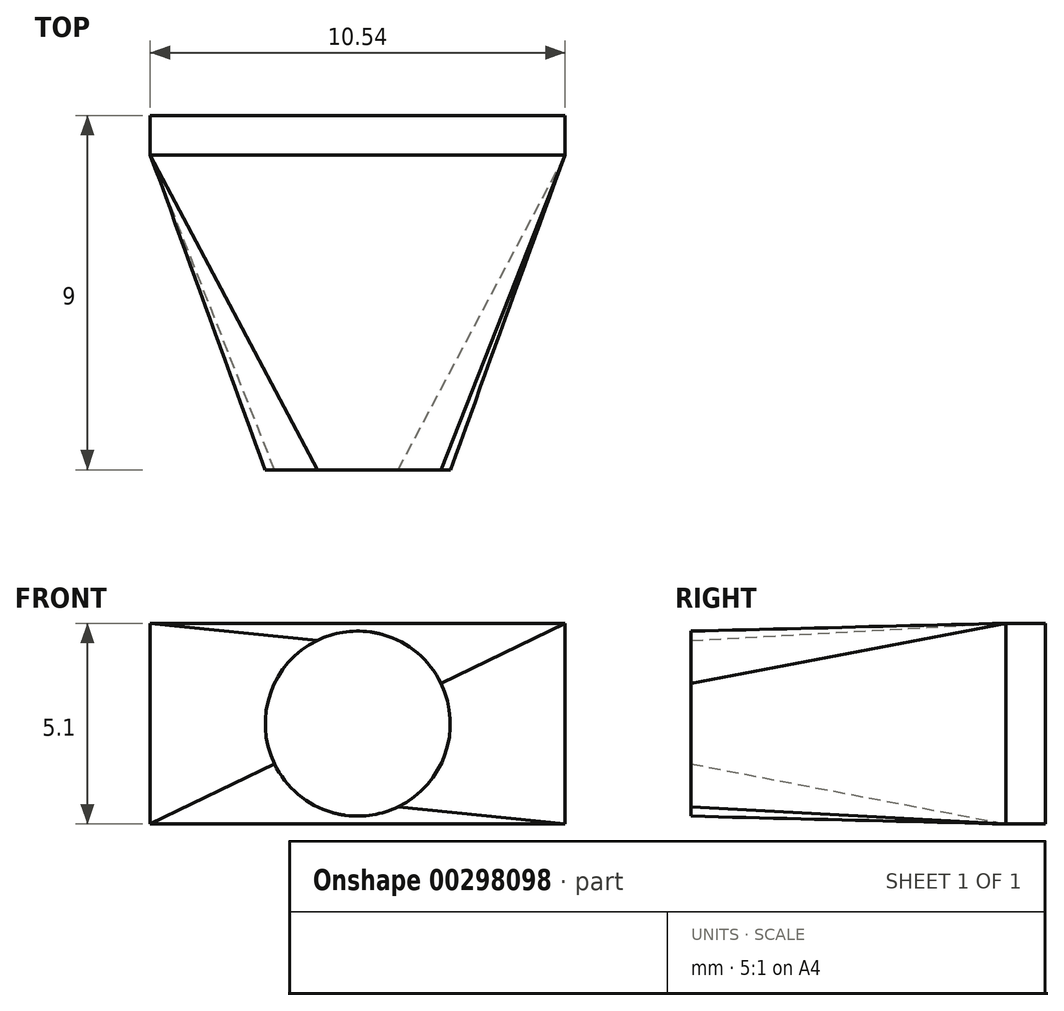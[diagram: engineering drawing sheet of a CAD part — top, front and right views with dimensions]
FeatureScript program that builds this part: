
annotation { "Feature Type Name" : "Feature", "Feature Type Description" : "" }
export const myFeature = defineFeature(function(context is Context, id is Id, definition is map)
    precondition{}
    {
        {
            var Q0;
            Q0=qCreatedBy(makeId("Front.planeOp"),FACE);
            var sketch = newSketch(context, id + "F0", { "sketchPlane" : qUnion([Q0])});
            skLineSegment(sketch, "E0.bottom", {"start": v(5.27, 2.55) * mm, "end": v(-5.27, 2.55) * mm});
            skLineSegment(sketch, "E0.top", {"start": v(5.27, -2.55) * mm, "end": v(-5.27, -2.55) * mm});
            skLineSegment(sketch, "E0.left", {"start": v(5.27, 2.55) * mm, "end": v(5.27, -2.55) * mm});
            skLineSegment(sketch, "E0.right", {"start": v(-5.27, 2.55) * mm, "end": v(-5.27, -2.55) * mm});
            skPoint(sketch, "E0.middle", {"position": v(0, 0) * mm});
            skSolve(sketch);
        }
        {
            var Q0;
            Q0=makeQuery(id+"F0.imprint","IMPRINT",FACE,{"disambiguationData":[TD([[makeQuery(id+"F0.imprint","IMPRINT",EDGE,{"derivedFrom":sQuery(id+"F0.wireOp",EDGE,"E0.bottom")}),1.0]])]});
            extrude(context, id + "F1", {"entities" : qUnion([Q0]), "depth" : 1 * mm});
        }
        {
            var Q0;
            Q0=makeQuery(id+"F1.opExtrude","CAP_FACE",FACE,{"disambiguationData":[OSD([sQuery(id+"F0.wireOp",EDGE,"E0.bottom"),sQuery(id+"F0.wireOp",EDGE,"E0.top"),sQuery(id+"F0.wireOp",EDGE,"E0.left"),sQuery(id+"F0.wireOp",EDGE,"E0.right")])],"isStart":false});
            cPlane(context, id + "F2", {"entities" : qUnion([Q0]), "cplaneType" : CPlaneType.OFFSET, "offset" : 8 * mm, "width" : 150 * mm, "height" : 150 * mm});
        }
        {
            var Q0;
            Q0=qCreatedBy(id+"F2.planeOp",FACE);
            var sketch = newSketch(context, id + "F3", { "sketchPlane" : qUnion([Q0])});
            skCircle(sketch, "E1", {"center": v(0, 0) * mm, "radius": 2.35 * mm});
            skSolve(sketch);
        }
        {
            var Q0;
            Q0=makeQuery(id+"F1.opExtrude","CAP_FACE",FACE,{"disambiguationData":[OSD([sQuery(id+"F0.wireOp",EDGE,"E0.bottom"),sQuery(id+"F0.wireOp",EDGE,"E0.top"),sQuery(id+"F0.wireOp",EDGE,"E0.left"),sQuery(id+"F0.wireOp",EDGE,"E0.right")])],"isStart":false});
            var sketch = newSketch(context, id + "F4", { "sketchPlane" : qUnion([Q0])});
            skLineSegment(sketch, "E2.0.0", {"start": v(-5.27, -2.55) * mm, "end": v(5.27, -2.55) * mm});
            skLineSegment(sketch, "E2.0.1", {"start": v(5.27, -2.55) * mm, "end": v(5.27, 2.55) * mm});
            skLineSegment(sketch, "E2.0.2", {"start": v(5.27, 2.55) * mm, "end": v(-5.27, 2.55) * mm});
            skLineSegment(sketch, "E2.0.3", {"start": v(-5.27, 2.55) * mm, "end": v(-5.27, -2.55) * mm});
            skSolve(sketch);
        }
        {
            var Q1;
            Q1=makeQuery(id+"F3.imprint","IMPRINT",FACE,{"disambiguationData":[TD([[makeQuery(id+"F3.imprint","IMPRINT",EDGE,{"derivedFrom":sQuery(id+"F3.wireOp",EDGE,"E1")}),1.0]])]});
            var Q2;
            Q2=makeQuery(id+"F4.imprint","IMPRINT",FACE,{"disambiguationData":[TD([[makeQuery(id+"F4.imprint","IMPRINT",EDGE,{"derivedFrom":sQuery(id+"F4.wireOp",EDGE,"E2.0.0")}),-1.0]])]});
            loft(context, id + "F5", {"operationType" : NewBodyOperationType.ADD, "sheetProfilesArray" : [{ "sheetProfileEntities" : qUnion([Q1]) }, { "sheetProfileEntities" : qUnion([Q2]) }]});
        }
    });
